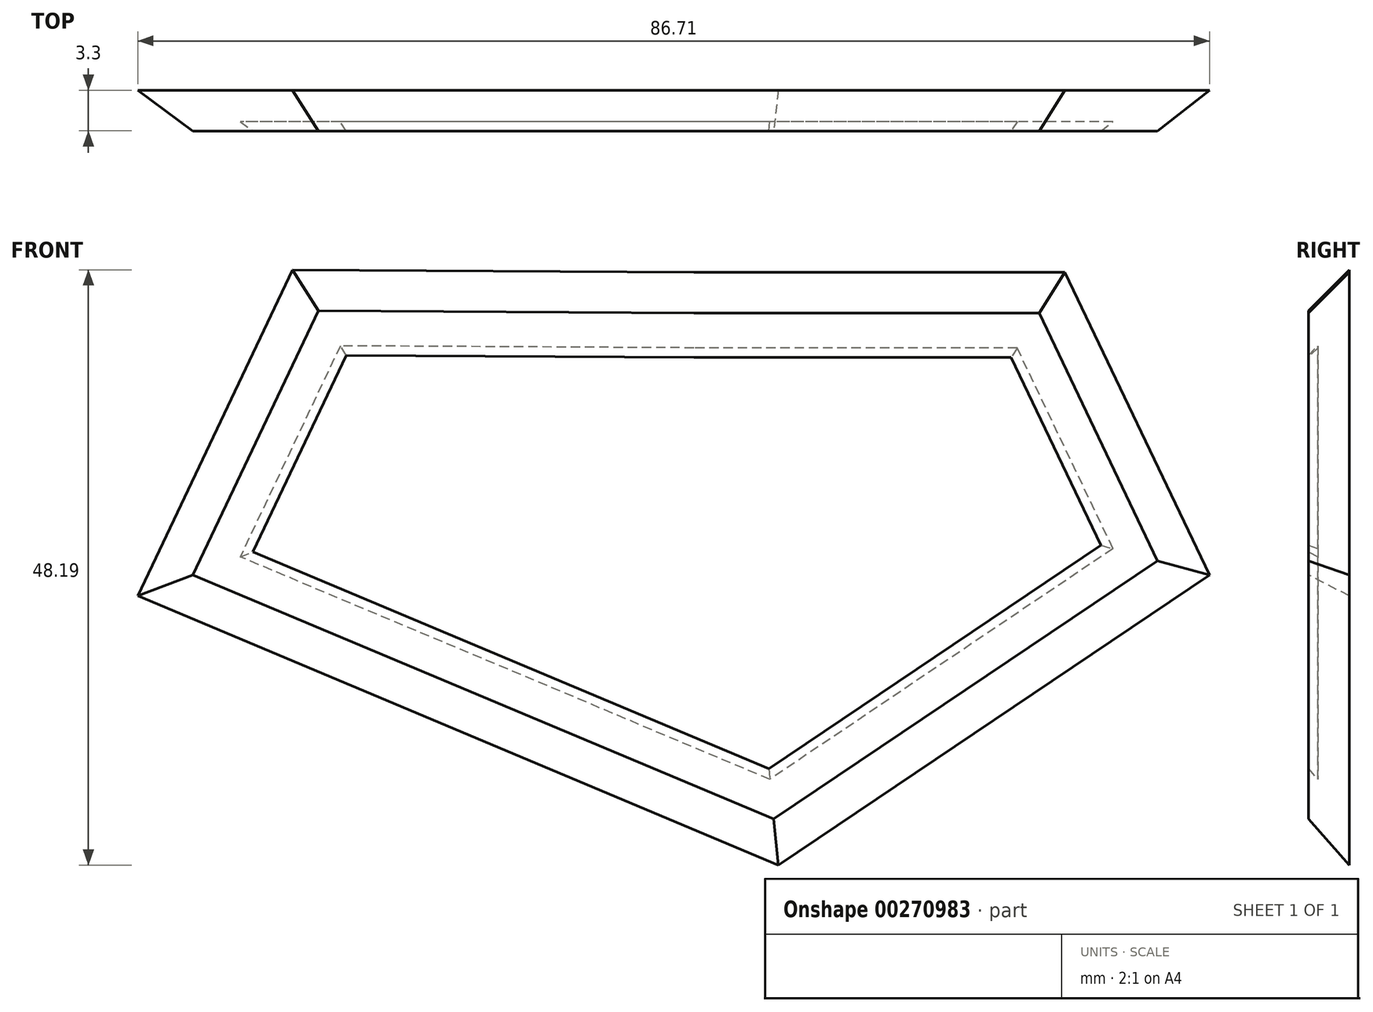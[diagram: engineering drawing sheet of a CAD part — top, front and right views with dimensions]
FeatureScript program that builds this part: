
annotation { "Feature Type Name" : "Feature", "Feature Type Description" : "" }
export const myFeature = defineFeature(function(context is Context, id is Id, definition is map)
    precondition{}
    {
        {
            var Q0;
            Q0=qCreatedBy(makeId("Front.planeOp"),FACE);
            var sketch = newSketch(context, id + "F0", { "sketchPlane" : qUnion([Q0])});
            skLineSegment(sketch, "E0", {"start": v(-54.14, -39.72) * mm, "end": v(-13.46, -39.72) * mm});
            skLineSegment(sketch, "E1", {"start": v(-13.46, -39.72) * mm, "end": v(-33.32, -12.8) * mm});
            skLineSegment(sketch, "E2", {"start": v(-33.32, -12.8) * mm, "end": v(-54.14, -39.72) * mm});
            skLineSegment(sketch, "E3", {"start": v(-54.14, -39.72) * mm, "end": v(-66.93, -12.6) * mm});
            skLineSegment(sketch, "E4", {"start": v(-66.93, -12.6) * mm, "end": v(-33.32, -12.8) * mm});
            skLineSegment(sketch, "E5", {"start": v(-33.32, -12.8) * mm, "end": v(-2.2, -12.8) * mm});
            skLineSegment(sketch, "E6", {"start": v(-2.2, -12.8) * mm, "end": v(-13.46, -39.72) * mm});
            skLineSegment(sketch, "E7", {"start": v(-13.46, -39.72) * mm, "end": v(-26.32, -64.59) * mm});
            skLineSegment(sketch, "E8", {"start": v(-26.32, -64.59) * mm, "end": v(-54.14, -39.72) * mm});
            skLineSegment(sketch, "E9", {"start": v(-26.32, -64.59) * mm, "end": v(10.65, -39.72) * mm});
            skLineSegment(sketch, "E10", {"start": v(10.65, -39.72) * mm, "end": v(-13.46, -39.72) * mm});
            skLineSegment(sketch, "E11", {"start": v(-2.2, -12.8) * mm, "end": v(10.65, -39.72) * mm});
            skLineSegment(sketch, "E12", {"start": v(-54.14, -39.72) * mm, "end": v(-80.74, -41.71) * mm});
            skLineSegment(sketch, "E13", {"start": v(-80.74, -41.71) * mm, "end": v(-66.93, -12.6) * mm});
            skLineSegment(sketch, "E14", {"start": v(-80.74, -41.71) * mm, "end": v(-26.32, -64.59) * mm});
            skSolve(sketch);
        }
        {
            var Q0;
            Q0 = qSketchRegion(id + "F0", true);
            extrude(context, id + "F1", {"entities" : qUnion([Q0]), "depth" : 3.3 * mm});
        }
        {
            var Q0;
            Q0=makeQuery(id+"F1.opExtrude","CAP_FACE",FACE,{"disambiguationData":[OSD([sQuery(id+"F0.wireOp",EDGE,"E4"),sQuery(id+"F0.wireOp",EDGE,"E5"),sQuery(id+"F0.wireOp",EDGE,"E9"),sQuery(id+"F0.wireOp",EDGE,"E11"),sQuery(id+"F0.wireOp",EDGE,"E13"),sQuery(id+"F0.wireOp",EDGE,"E14")])],"isStart":false});
            chamfer(context, id + "F2", {"entities" : qUnion([Q0]), "width" : 5.08 * mm, "tangentPropagation" : true});
        }
        {
            var Q0;
            Q0=makeQuery(id+"F1.opExtrude","CAP_FACE",FACE,{"disambiguationData":[OSD([sQuery(id+"F0.wireOp",EDGE,"E4"),sQuery(id+"F0.wireOp",EDGE,"E5"),sQuery(id+"F0.wireOp",EDGE,"E9"),sQuery(id+"F0.wireOp",EDGE,"E11"),sQuery(id+"F0.wireOp",EDGE,"E13"),sQuery(id+"F0.wireOp",EDGE,"E14")])],"isStart":false});
            shell(context, id + "F3", {"entities" : qUnion([Q0]), "thickness" : 2.54 * mm});
        }
    });
